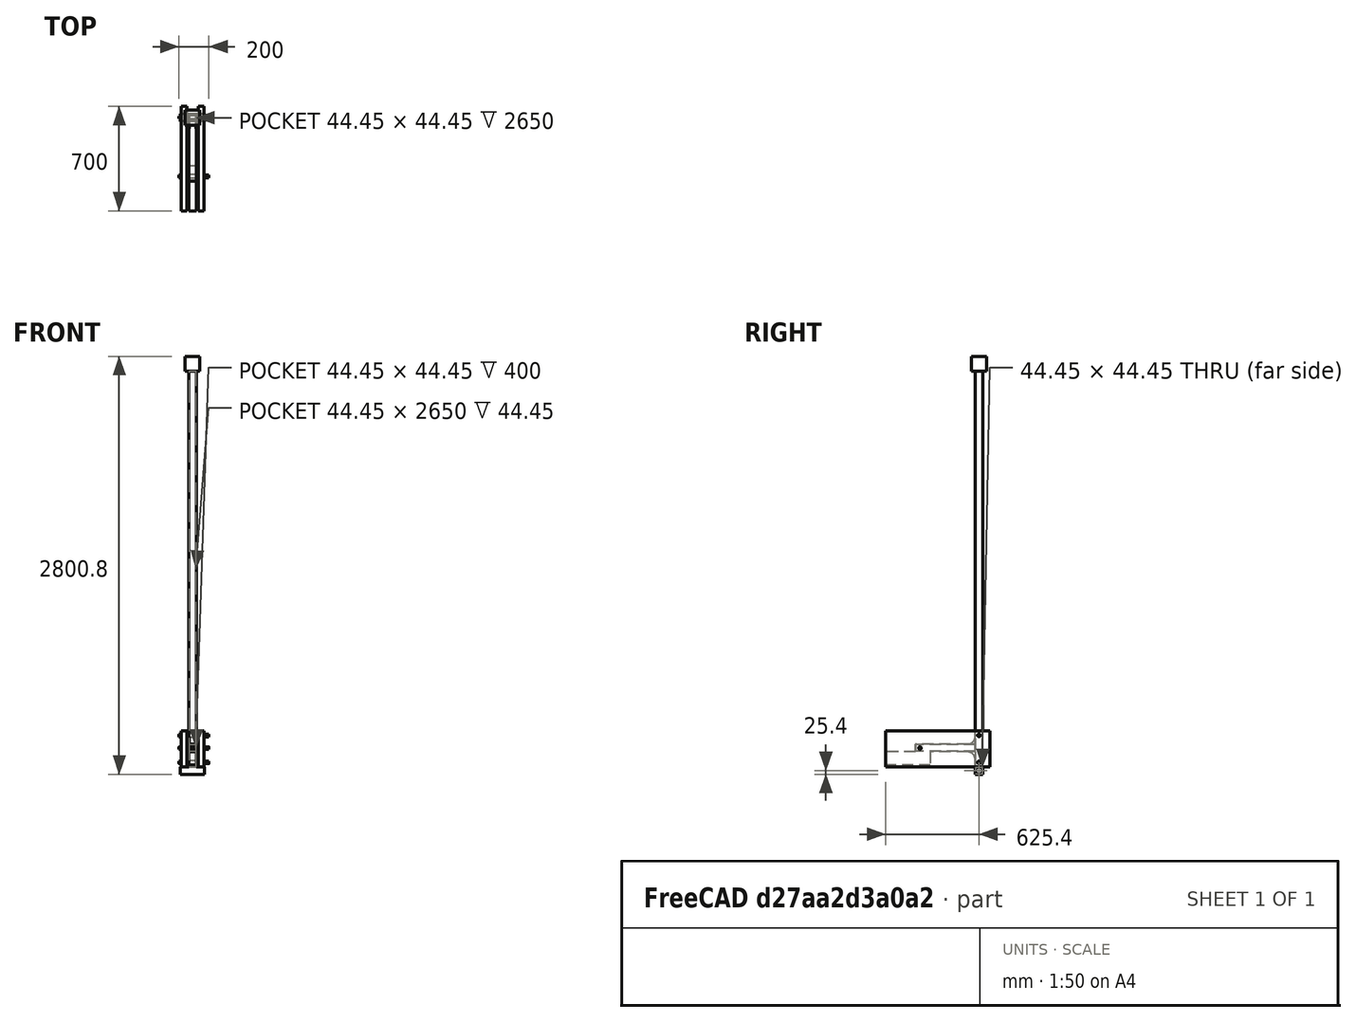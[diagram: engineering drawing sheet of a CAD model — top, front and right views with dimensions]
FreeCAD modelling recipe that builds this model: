
FCSTD DOCUMENT  (FreeCAD 0.16R6706 (Git))
Label: deckPost
License: All rights reserved
LicenseURL: http://en.wikipedia.org/wiki/All_rights_reserved
objects: Sketcher::SketchObject×19, PartDesign::Pad×19, Part::MultiFuse×6, Part::Cut×3, Part::Part2DObjectPython×2, Fem::ConstraintForce×2, Spreadsheet::Sheet×1, App::DocumentObjectGroup×1, Fem::FemSolverObjectPython×1, App::MaterialObjectPython×1, Part::Box×1, Fem::ConstraintFixed×1, Fem::FemAnalysisPython×1
note: 69 computed .brp shape members not serialized (recipe doc carries the construction recipe); baked Part::Feature solids carry a one-line shape summary decoded from their .brp

FEATURE [Sketcher::SketchObject] Sketch  label="TubeSketch"
  expr: Constraints[19] = Spreadsheet.wallThickness
  expr: Constraints[20] = Spreadsheet.wallThickness
  expr: Constraints[21] = Spreadsheet.outerWidth
  expr: Constraints[18] = Spreadsheet.wallThickness
  sketch-geometry (8):
    g0: LineSegment StartX=0 StartY=50.8 StartZ=0 EndX=50.8 EndY=50.8 EndZ=0
    g1: LineSegment StartX=50.8 StartY=50.8 StartZ=0 EndX=50.8 EndY=0 EndZ=0
    g2: LineSegment StartX=50.8 StartY=0 StartZ=0 EndX=0 EndY=0 EndZ=0
    g3: LineSegment StartX=0 StartY=0 StartZ=0 EndX=0 EndY=50.8 EndZ=0
    g4: LineSegment StartX=3.175 StartY=47.625 StartZ=0 EndX=47.625 EndY=47.625 EndZ=0
    g5: LineSegment StartX=47.625 StartY=47.625 StartZ=0 EndX=47.625 EndY=3.175 EndZ=0
    g6: LineSegment StartX=47.625 StartY=3.175 StartZ=0 EndX=3.175 EndY=3.175 EndZ=0
    g7: LineSegment StartX=3.175 StartY=3.175 StartZ=0 EndX=3.175 EndY=47.625 EndZ=0
  constraints (23):
    c: Coincident(g0,g1)
    c: Coincident(g1,g2)
    c: Coincident(g2,g3)
    c: Coincident(g3,g0)
    c: Horizontal(g0)
    c: Horizontal(g2)
    c: Vertical(g1)
    c: Vertical(g3)
    c: Coincident(g4,g5)
    c: Coincident(g5,g6)
    c: Coincident(g6,g7)
    c: Coincident(g7,g4)
    c: Horizontal(g4)
    c: Horizontal(g6)
    c: Vertical(g5)
    c: Vertical(g7)
    c: Equal(g0,g3)
    c: Equal(g4,g7)
    c: DistanceX(g0,g4) = 3.175
    c: DistanceY(g4,g0) = 3.175
    c: DistanceX(g5,g1) = 3.175
    c: Distance(g0,g0) = 50.8
    c: Coincident(g2,g-1)
FEATURE [PartDesign::Pad] Pad  label="Post"
  Length = 2650
  Length2 = 100
  Sketch = -> Sketch
  Type = 0
  expr: Length = Spreadsheet.postLength
FEATURE [Spreadsheet::Sheet] Spreadsheet
  cells = J2=N; K2=lbf; L2=Resultant Force lbf; A3=Tube Wall Thickness; B3(wallThickness)=3.175; C3==Spreadsheet.wallThickness; I3=Post Top Medial Force; J3(medialForce)=350; K3==medialForce / 9.810000000000001; L3==sqrt(Spreadsheet.medialForce ^ 2 + Spreadsheet.lateralForce ^ 2) / 9.810000000000001 * 2.2; A4=Tube Outer Width; B4(outerWidth)=50.8; C4==Spreadsheet.outerWidth; I4=8ft Post Lateral Force; J4(lateralForce)=350; K4==lateralForce / 9.810000000000001; A5=Brace Height; B5(braceHeight)=100; C5==Spreadsheet.braceHeight; A6=Brace Length; B6(braceLength)=400; C6==Spreadsheet.braceLength; A7=Bolt Hole Diam; B7(boltHoleDiam)=17; C7==Spreadsheet.boltHoleDiam; A8=Bolt Tube Thickness; B8(boltTubeThick)=3.175; C8==Spreadsheet.boltTubeThick; A9=Gusset Thickness; B9(gussetThickness)=3.175; C9==Spreadsheet.gussetThickness; A10=Upper Bolt Height; B10(upperBoltHeight)=210; C10==Spreadsheet.upperBoltHeight; D10==Spreadsheet.joistWidth - Spreadsheet.upperBoltHeight - Spreadsheet.boltHoleDiam / 2; E10==Spreadsheet.joistWidth - Spreadsheet.upperBoltHeight - Spreadsheet.boltHoleDiam / 2; F10=Distance from upper bolt hole to joist upper edge ; A11=Lower Bolt Height; B11(lowerBoltHeight)=30; C11==Spreadsheet.lowerBoltHeight; D11==Spreadsheet.lowerBoltHeight - Spreadsheet.boltHoleDiam / 2; E11==Spreadsheet.lowerBoltHeight - Spreadsheet.boltHoleDiam / 2; F11=Distance from lower bolt hole to joist lower edge; A12=Total Post Length; B12(postLength)=2650; C12==Spreadsheet.postLength; D12(postEffortArm)==Spreadsheet.postLength - Spreadsheet.joistWidth - Spreadsheet.deckThickness; E12==Spreadsheet.postLength - Spreadsheet.joistWidth - Spreadsheet.deckThickness; F12=Height Above Finished Deck; A13=2x10 Joist Width; B13(joistWidth)=241.3; C13==Spreadsheet.joistWidth; A14=Deck Thickness; B14(deckThickness)=19.05; C14==Spreadsheet.deckThickness; A15=Gusset Raduis; B15(gussetRadius)=75; C15==Spreadsheet.gussetRadius; A16=Gusset Length; B16(gussetLength)=50; C16==Spreadsheet.gussetLength; C19=Al 6061 - 0; D19=Al 6061 - T6; E19=ASTM A500 Steel Hot Rolled; I19=Douglas Fir; A20=Young's Modulus; C20==69GPa; D20==69GPa; E20==200GPa; I20==12.17GPa; A21=Poisson's Ratio; C21=0.33; D21=0.33; E21=0.29; I21=0.02; A22=Density; C22=2.7e-006; D22=2.7e-006; E22==7.85g / cm ^ 3; I22==510kg / m ^ 3; A23=Yield Strength; C23==55.2MPa; D23==276MPa; E23==270MPa; I23==3MPa; A24=Web Site; C24=http://www.matweb.com/search/DataSheet.aspx?MatGUID=626ec8cdca604f1994be4fc2bc6f7f63&ckck=1; D24=http://www.matweb.com/search/DataSheet.aspx?MatGUID=b8d536e0b9b54bd7b69e4124d8f1d20a; I24=http://www.wood-database.com/douglas-fir/
FEATURE [Sketcher::SketchObject] Sketch002  label="GussetSketch"
  Placement = pos=(0,0,150.8) rot=(0.57735,0.57735,0.57735;2.0944rad)
  expr: Constraints[9] = Spreadsheet.gussetRadius
  expr: Constraints[6] = Spreadsheet.gussetLength
  expr: Constraints[5] = Spreadsheet.gussetLength
  expr: Placement.Base.z = Spreadsheet.braceHeight + Spreadsheet.outerWidth
  sketch-geometry (3):
    g0: LineSegment StartX=0 StartY=0 StartZ=0 EndX=0 EndY=50 EndZ=0
    g1: LineSegment StartX=0 StartY=0 StartZ=0 EndX=-50 EndY=0 EndZ=0
    g2: ArcOfCircle CenterX=-53.033 CenterY=53.033 CenterZ=0 NormalX=0 NormalY=0 NormalZ=1 Radius=53.1197 StartAngle=4.76952 EndAngle=6.22606
  constraints (10):
    c: Vertical(g0)
    c: Coincident(g1,g0)
    c: PointOnObject(g1,g-1)
    c: Horizontal(g1)
    c: PointOnObject(g0,g-2)
    c: Distance(g0) = 50
    c: Distance(g1) = 50
    c: Coincident(g2,g0)
    c: Coincident(g2,g1)
    c: Distance(g-1,g2) = 75
FEATURE [PartDesign::Pad] Pad002  label="Gusset1"
  Length = 3.175
  Length2 = 100
  Placement = pos=(0,0,150.8) rot=(0.57735,0.57735,0.57735;2.0944rad)
  Sketch = -> Sketch002
  Type = 0
  expr: Length = Spreadsheet.gussetThickness
FEATURE [Sketcher::SketchObject] MirroredSketch
  Placement = pos=(0,0,100) rot=(0.57735,0.57735,0.57735;2.0944rad)
  expr: Constraints[3] = Spreadsheet.gussetLength
  expr: Constraints[7] = Spreadsheet.gussetRadius
  expr: Constraints[8] = Spreadsheet.gussetLength
  sketch-geometry (3):
    g0: LineSegment StartX=0 StartY=0 StartZ=0 EndX=0 EndY=-50 EndZ=0
    g1: LineSegment StartX=0 StartY=0 StartZ=0 EndX=-50 EndY=0 EndZ=0
    g2: ArcOfCircle CenterX=-53.033 CenterY=-53.033 CenterZ=0 NormalX=0 NormalY=0 NormalZ=1 Radius=53.1197 StartAngle=0.0571287 EndAngle=1.51367
  constraints (9):
    c: Vertical(g0)
    c: Coincident(g1,g0)
    c: Horizontal(g1)
    c: Distance(g0) = 50
    c: Coincident(g2,g0)
    c: Coincident(g0,g-1)
    c: Coincident(g1,g2)
    c: Distance(g-1,g2) = 75
    c: Distance(g1) = 50
FEATURE [PartDesign::Pad] Pad004  label="Gusset2"
  Length = 3.175
  Length2 = 100
  Placement = pos=(0,0,100) rot=(0.57735,0.57735,0.57735;2.0944rad)
  Sketch = -> MirroredSketch
  Type = 0
  expr: Length = Spreadsheet.gussetThickness
FEATURE [Sketcher::SketchObject] Sketch003  label="GussetSketch001"
  Placement = pos=(47.625,0,150.8) rot=(0.57735,0.57735,0.57735;2.0944rad)
  expr: Constraints[9] = Spreadsheet.gussetRadius
  expr: Placement.Base.x = Spreadsheet.outerWidth - Spreadsheet.gussetThickness
  expr: Constraints[6] = Spreadsheet.gussetLength
  expr: Constraints[5] = Spreadsheet.gussetLength
  expr: Placement.Base.z = Spreadsheet.braceHeight + Spreadsheet.outerWidth
  sketch-geometry (3):
    g0: LineSegment StartX=0 StartY=0 StartZ=0 EndX=0 EndY=50 EndZ=0
    g1: LineSegment StartX=0 StartY=0 StartZ=0 EndX=-50 EndY=0 EndZ=0
    g2: ArcOfCircle CenterX=-53.033 CenterY=53.033 CenterZ=0 NormalX=0 NormalY=0 NormalZ=1 Radius=53.1197 StartAngle=4.76952 EndAngle=6.22606
  constraints (10):
    c: Vertical(g0)
    c: Coincident(g1,g0)
    c: PointOnObject(g1,g-1)
    c: Horizontal(g1)
    c: PointOnObject(g0,g-2)
    c: Distance(g0) = 50
    c: Distance(g1) = 50
    c: Coincident(g2,g0)
    c: Coincident(g1,g2)
    c: Distance(g-1,g2) = 75
FEATURE [PartDesign::Pad] Pad005  label="Gusset3"
  Length = 3.175
  Length2 = 100
  Placement = pos=(47.625,0,150.8) rot=(0.57735,0.57735,0.57735;2.0944rad)
  Sketch = -> Sketch003
  Type = 0
  expr: Length = Spreadsheet.gussetThickness
FEATURE [Sketcher::SketchObject] MirroredSketch001
  Placement = pos=(47.625,0,100) rot=(0.57735,0.57735,0.57735;2.0944rad)
  expr: Constraints[8] = Spreadsheet.gussetRadius
  expr: Constraints[3] = Spreadsheet.gussetLength
  expr: Constraints[4] = Spreadsheet.gussetLength
  expr: Placement.Base.x = Spreadsheet.outerWidth - Spreadsheet.gussetThickness
  sketch-geometry (3):
    g0: LineSegment StartX=0 StartY=0 StartZ=0 EndX=0 EndY=-50 EndZ=0
    g1: LineSegment StartX=0 StartY=0 StartZ=0 EndX=-50 EndY=0 EndZ=0
    g2: ArcOfCircle CenterX=-53.033 CenterY=-53.033 CenterZ=0 NormalX=0 NormalY=0 NormalZ=1 Radius=53.1197 StartAngle=0.0571287 EndAngle=1.51367
  constraints (9):
    c: Vertical(g0)
    c: Coincident(g1,g0)
    c: Horizontal(g1)
    c: Distance(g0) = 50
    c: Distance(g1) = 50
    c: Coincident(g2,g1)
    c: Coincident(g0,g2)
    c: Coincident(g0,g-1)
    c: Distance(g-1,g2) = 75
FEATURE [PartDesign::Pad] Pad006  label="Gusset4"
  Length = 3.175
  Length2 = 100
  Placement = pos=(47.625,0,100) rot=(0.57735,0.57735,0.57735;2.0944rad)
  Sketch = -> MirroredSketch001
  Type = 0
  expr: Length = Spreadsheet.gussetThickness
FEATURE [Sketcher::SketchObject] Sketch004  label="Brace Bolt Tube Sketch"
  Placement = pos=(0,-370,125.4) rot=(0,1,0;1.5708rad)
  expr: Placement.Base.z = Spreadsheet.braceHeight + Spreadsheet.outerWidth / 2
  expr: Placement.Base.y = -Spreadsheet.braceLength + 30
  expr: Constraints[3] = Spreadsheet.boltHoleDiam / 2 + Spreadsheet.boltTubeThick
  expr: Constraints[2] = Spreadsheet.boltHoleDiam / 2
  sketch-geometry (2):
    g0: Circle CenterX=0 CenterY=0 CenterZ=0 NormalX=0 NormalY=0 NormalZ=1 Radius=8.5
    g1: Circle CenterX=0 CenterY=0 CenterZ=0 NormalX=0 NormalY=0 NormalZ=1 Radius=11.675
  constraints (4):
    c: Coincident(g0,g-1)
    c: Coincident(g1,g-1)
    c: Radius(g0) = 8.5
    c: Radius(g1) = 11.675
FEATURE [Part::Part2DObjectPython] Line  label="Brace Center"  # Draft 2D object (typed FeaturePython)
  ChamferSize = 0
  Closed = false
  End = (0,-300,131.75)
  FilletRadius = 0
  Length = 300
  MakeFace = false
  Placement = pos=(0,0,0) rot=(0,-1,0;1.5708rad)
  Points = (2) [(131.75,-8.10463e-15,2.92544e-14),(131.75,-300,-3.7359e-14)]
  Start = (0,0,131.75)
  Subdivisions = 0
FEATURE [Part::Part2DObjectPython] Line001  label="Post Ceenter"  # Draft 2D object (typed FeaturePython)
  ChamferSize = 0
  Closed = false
  End = (0,31.75,2500)
  FilletRadius = 0
  Length = 2500
  MakeFace = false
  Placement = pos=(0,0,0) rot=(0,-1,0;1.5708rad)
  Points = (2) [(0,31.75,0),(2500,31.75,5.62161e-13)]
  Start = (0,31.75,0)
  Subdivisions = 0
FEATURE [App::DocumentObjectGroup] Construction
  Group = -> [Line,Line001]
FEATURE [PartDesign::Pad] Pad007  label="Brace Bolt Tube"
  Length = 50.8
  Length2 = 100
  Placement = pos=(0,-370,125.4) rot=(0,1,0;1.5708rad)
  Sketch = -> Sketch004
  Type = 0
  expr: Length = Spreadsheet.outerWidth
FEATURE [Sketcher::SketchObject] Sketch005  label="Bolt Hole Sketch"
  Placement = pos=(0,-370,125.4) rot=(0,1,0;1.5708rad)
  expr: Placement.Base.y = -Spreadsheet.braceLength + 30
  expr: Placement.Base.z = Spreadsheet.braceHeight + Spreadsheet.outerWidth / 2
  sketch-geometry (1):
    g0: Circle CenterX=0 CenterY=0 CenterZ=0 NormalX=0 NormalY=0 NormalZ=1 Radius=9
  constraints (2):
    c: Coincident(g0,g-1)
    c: Radius(g0) = 9
FEATURE [PartDesign::Pad] Pad008  label="Brace Bolt Hole"
  Length = 50.8
  Length2 = 100
  Placement = pos=(0,-370,125.4) rot=(0,1,0;1.5708rad)
  Sketch = -> Sketch005
  Type = 0
  expr: Length = Spreadsheet.outerWidth
FEATURE [Sketcher::SketchObject] Sketch006  label="Lower Bolt Tube Sketch"
  Placement = pos=(0,25.4,30) rot=(0,1,0;1.5708rad)
  expr: Placement.Base.y = Spreadsheet.outerWidth / 2
  expr: Constraints[3] = Spreadsheet.boltHoleDiam / 2 + Spreadsheet.boltTubeThick
  expr: Constraints[2] = Spreadsheet.boltHoleDiam / 2
  sketch-geometry (2):
    g0: Circle CenterX=0 CenterY=0 CenterZ=0 NormalX=0 NormalY=0 NormalZ=1 Radius=8.5
    g1: Circle CenterX=0 CenterY=0 CenterZ=0 NormalX=0 NormalY=0 NormalZ=1 Radius=11.675
  constraints (4):
    c: Coincident(g0,g-1)
    c: Coincident(g1,g-1)
    c: Radius(g0) = 8.5
    c: Radius(g1) = 11.675
FEATURE [PartDesign::Pad] Pad009  label="Lower Bolt Tube"
  Length = 50.8
  Length2 = 100
  Placement = pos=(0,25.4,30) rot=(0,1,0;1.5708rad)
  Sketch = -> Sketch006
  Type = 0
  expr: Length = Spreadsheet.outerWidth
FEATURE [Sketcher::SketchObject] Sketch007  label="Upper Bolt Tube Sketch"
  Placement = pos=(0,25.4,210) rot=(0,1,0;1.5708rad)
  expr: Placement.Base.z = Spreadsheet.upperBoltHeight
  expr: Placement.Base.y = Spreadsheet.outerWidth / 2
  expr: Constraints[3] = Spreadsheet.boltHoleDiam / 2 + Spreadsheet.boltTubeThick
  expr: Constraints[2] = Spreadsheet.boltHoleDiam / 2
  sketch-geometry (2):
    g0: Circle CenterX=0 CenterY=0 CenterZ=0 NormalX=0 NormalY=0 NormalZ=1 Radius=8.5
    g1: Circle CenterX=0 CenterY=0 CenterZ=0 NormalX=0 NormalY=0 NormalZ=1 Radius=11.675
  constraints (4):
    c: Coincident(g0,g-1)
    c: Coincident(g1,g-1)
    c: Radius(g0) = 8.5
    c: Radius(g1) = 11.675
FEATURE [PartDesign::Pad] Pad010  label="Upper Bolt Tube"
  Length = 50.8
  Length2 = 100
  Placement = pos=(0,25.4,210) rot=(0,1,0;1.5708rad)
  Sketch = -> Sketch007
  Type = 0
  expr: Length = Spreadsheet.outerWidth
FEATURE [Sketcher::SketchObject] Sketch001  label="BraceTubeSketch"
  Placement = pos=(0,0,100) rot=(1,0,0;1.5708rad)
  expr: Placement.Base.z = Spreadsheet.braceHeight
  expr: Constraints[19] = Spreadsheet.wallThickness
  expr: Constraints[20] = Spreadsheet.wallThickness
  expr: Constraints[21] = Spreadsheet.outerWidth
  expr: Constraints[18] = Spreadsheet.wallThickness
  sketch-geometry (8):
    g0: LineSegment StartX=0 StartY=50.8 StartZ=0 EndX=50.8 EndY=50.8 EndZ=0
    g1: LineSegment StartX=50.8 StartY=50.8 StartZ=0 EndX=50.8 EndY=0 EndZ=0
    g2: LineSegment StartX=50.8 StartY=0 StartZ=0 EndX=0 EndY=0 EndZ=0
    g3: LineSegment StartX=0 StartY=0 StartZ=0 EndX=0 EndY=50.8 EndZ=0
    g4: LineSegment StartX=3.175 StartY=47.625 StartZ=0 EndX=47.625 EndY=47.625 EndZ=0
    g5: LineSegment StartX=47.625 StartY=47.625 StartZ=0 EndX=47.625 EndY=3.175 EndZ=0
    g6: LineSegment StartX=47.625 StartY=3.175 StartZ=0 EndX=3.175 EndY=3.175 EndZ=0
    g7: LineSegment StartX=3.175 StartY=3.175 StartZ=0 EndX=3.175 EndY=47.625 EndZ=0
  constraints (23):
    c: Coincident(g0,g1)
    c: Coincident(g1,g2)
    c: Coincident(g2,g3)
    c: Coincident(g3,g0)
    c: Horizontal(g0)
    c: Horizontal(g2)
    c: Vertical(g1)
    c: Vertical(g3)
    c: Coincident(g4,g5)
    c: Coincident(g5,g6)
    c: Coincident(g6,g7)
    c: Coincident(g7,g4)
    c: Horizontal(g4)
    c: Horizontal(g6)
    c: Vertical(g5)
    c: Vertical(g7)
    c: Equal(g0,g3)
    c: Equal(g4,g7)
    c: DistanceX(g0,g4) = 3.175
    c: DistanceY(g4,g0) = 3.175
    c: DistanceX(g5,g1) = 3.175
    c: Distance(g0,g0) = 50.8
    c: Coincident(g2,g-1)
FEATURE [PartDesign::Pad] Pad001  label="Brace"
  Length = 400
  Length2 = 100
  Placement = pos=(0,0,100) rot=(1,0,0;1.5708rad)
  Sketch = -> Sketch001
  Type = 0
  expr: Length = Spreadsheet.braceLength
FEATURE [Part::Cut] Cut  label="Brace Cut"
  Base = -> Pad001
  Tool = -> Pad008
FEATURE [Sketcher::SketchObject] Sketch008  label="Lower Bolt Hole Sketch"
  Placement = pos=(0,25.4,30) rot=(0,1,0;1.5708rad)
  expr: Placement.Base.y = Spreadsheet.outerWidth / 2
  sketch-geometry (1):
    g0: Circle CenterX=0 CenterY=0 CenterZ=0 NormalX=0 NormalY=0 NormalZ=1 Radius=9
  constraints (2):
    c: Coincident(g0,g-1)
    c: Radius(g0) = 9
FEATURE [PartDesign::Pad] Pad011  label="Lower Bolt Hole"
  Length = 50.8
  Length2 = 100
  Placement = pos=(0,25.4,30) rot=(0,1,0;1.5708rad)
  Sketch = -> Sketch008
  Type = 0
  expr: Length = Spreadsheet.outerWidth
FEATURE [Part::Cut] Cut001
  Base = -> Pad
  Tool = -> Pad011
FEATURE [Sketcher::SketchObject] Sketch009  label="Upper Bolt Hole Sketch"
  Placement = pos=(0,25.4,210) rot=(0,1,0;1.5708rad)
  expr: Placement.Base.z = Spreadsheet.upperBoltHeight
  expr: Placement.Base.y = Spreadsheet.outerWidth / 2
  sketch-geometry (1):
    g0: Circle CenterX=0 CenterY=0 CenterZ=0 NormalX=0 NormalY=0 NormalZ=1 Radius=9
  constraints (2):
    c: Coincident(g0,g-1)
    c: Radius(g0) = 9
FEATURE [PartDesign::Pad] Pad012  label="Upper Bolt Hole"
  Length = 50.8
  Length2 = 100
  Placement = pos=(0,25.4,210) rot=(0,1,0;1.5708rad)
  Sketch = -> Sketch009
  Type = 0
  expr: Length = Spreadsheet.outerWidth
FEATURE [Part::Cut] Cut002  label="Post Cut"
  Base = -> Cut001
  Tool = -> Pad012
FEATURE [Part::MultiFuse] Fusion  label="Brace Fusion"
  Shapes = -> [Cut,Pad007]
FEATURE [Part::MultiFuse] Fusion001  label="Post Fusion"
  Shapes = -> [Cut002,Pad009,Pad010]
FEATURE [Part::MultiFuse] Fusion002  label="Post and Bracket"
  Shapes = -> [Pad006,Pad005,Pad004,Pad002,Fusion,Fusion001]
FEATURE [Sketcher::SketchObject] Sketch010  label="Joist Sketch"
  Placement = pos=(-50.8,100,0) rot=(1,0,0;1.5708rad)
  expr: Placement.Base.x = -1.5in - 0.5in
  expr: Constraints[10] = Spreadsheet.joistWidth
  sketch-geometry (4):
    g0: LineSegment StartX=0 StartY=0 StartZ=0 EndX=38.1 EndY=0 EndZ=0
    g1: LineSegment StartX=38.1 StartY=0 StartZ=0 EndX=38.1 EndY=241.3 EndZ=0
    g2: LineSegment StartX=38.1 StartY=241.3 StartZ=0 EndX=0 EndY=241.3 EndZ=0
    g3: LineSegment StartX=0 StartY=241.3 StartZ=0 EndX=0 EndY=0 EndZ=0
  constraints (11):
    c: Coincident(g0,g1)
    c: Coincident(g1,g2)
    c: Coincident(g2,g3)
    c: Coincident(g3,g0)
    c: Horizontal(g0)
    c: Horizontal(g2)
    c: Vertical(g1)
    c: Vertical(g3)
    c: Coincident(g0,g-1)
    c: Distance(g2) = 38.1
    c: Distance(g3) = 241.3
FEATURE [PartDesign::Pad] Pad013  label="Joist"
  Length = 700
  Length2 = 100
  Placement = pos=(-50.8,100,0) rot=(1,0,0;1.5708rad)
  Sketch = -> Sketch010
  Type = 0
FEATURE [Sketcher::SketchObject] Sketch011  label="Brace Bolt Sketch"
  Placement = pos=(-65,-370,125.4) rot=(0,1,0;1.5708rad)
  expr: Placement.Base.y = -Spreadsheet.braceLength + 30
  expr: Placement.Base.z = Spreadsheet.braceHeight + Spreadsheet.outerWidth / 2
  sketch-geometry (1):
    g0: Circle CenterX=0 CenterY=0 CenterZ=0 NormalX=0 NormalY=0 NormalZ=1 Radius=9
  constraints (2):
    c: Coincident(g0,g-1)
    c: Radius(g0) = 9
FEATURE [PartDesign::Pad] Pad014  label="Brace Bolt"
  Length = 200
  Length2 = 100
  Placement = pos=(-65,-370,125.4) rot=(0,1,0;1.5708rad)
  Sketch = -> Sketch011
  Type = 0
FEATURE [Sketcher::SketchObject] Sketch012  label="Upper Bolt Sketch"
  Placement = pos=(-65,25.4,210) rot=(0,1,0;1.5708rad)
  expr: Placement.Base.y = Spreadsheet.outerWidth / 2
  expr: Placement.Base.z = Spreadsheet.upperBoltHeight
  sketch-geometry (1):
    g0: Circle CenterX=0 CenterY=0 CenterZ=0 NormalX=0 NormalY=0 NormalZ=1 Radius=9
  constraints (2):
    c: Coincident(g0,g-1)
    c: Radius(g0) = 9
FEATURE [PartDesign::Pad] Pad015  label="Upper Bolt"
  Length = 200
  Length2 = 100
  Placement = pos=(-65,25.4,210) rot=(0,1,0;1.5708rad)
  Sketch = -> Sketch012
  Type = 0
FEATURE [Sketcher::SketchObject] Sketch013  label="Lower Bolt Sketch"
  Placement = pos=(-65,25.4,30) rot=(0,1,0;1.5708rad)
  expr: Placement.Base.y = Spreadsheet.outerWidth / 2
  expr: Placement.Base.z = Spreadsheet.lowerBoltHeight
  sketch-geometry (1):
    g0: Circle CenterX=0 CenterY=0 CenterZ=0 NormalX=0 NormalY=0 NormalZ=1 Radius=9
  constraints (2):
    c: Coincident(g0,g-1)
    c: Radius(g0) = 9
FEATURE [PartDesign::Pad] Pad016  label="Lower Bolt"
  Length = 200
  Length2 = 100
  Placement = pos=(-65,25.4,30) rot=(0,1,0;1.5708rad)
  Sketch = -> Sketch013
  Type = 0
FEATURE [Sketcher::SketchObject] Sketch014  label="Lower support Tube Sketch"
  Placement = pos=(105,0,0) rot=(0,1,0;1.5708rad)
  expr: Constraints[19] = Spreadsheet.wallThickness
  expr: Constraints[20] = Spreadsheet.wallThickness
  expr: Constraints[21] = Spreadsheet.outerWidth
  expr: Constraints[18] = Spreadsheet.wallThickness
  sketch-geometry (8):
    g0: LineSegment StartX=0 StartY=50.8 StartZ=0 EndX=50.8 EndY=50.8 EndZ=0
    g1: LineSegment StartX=50.8 StartY=50.8 StartZ=0 EndX=50.8 EndY=0 EndZ=0
    g2: LineSegment StartX=50.8 StartY=0 StartZ=0 EndX=0 EndY=0 EndZ=0
    g3: LineSegment StartX=0 StartY=0 StartZ=0 EndX=0 EndY=50.8 EndZ=0
    g4: LineSegment StartX=3.175 StartY=47.625 StartZ=0 EndX=47.625 EndY=47.625 EndZ=0
    g5: LineSegment StartX=47.625 StartY=47.625 StartZ=0 EndX=47.625 EndY=3.175 EndZ=0
    g6: LineSegment StartX=47.625 StartY=3.175 StartZ=0 EndX=3.175 EndY=3.175 EndZ=0
    g7: LineSegment StartX=3.175 StartY=3.175 StartZ=0 EndX=3.175 EndY=47.625 EndZ=0
  constraints (23):
    c: Coincident(g0,g1)
    c: Coincident(g1,g2)
    c: Coincident(g2,g3)
    c: Coincident(g3,g0)
    c: Horizontal(g0)
    c: Horizontal(g2)
    c: Vertical(g1)
    c: Vertical(g3)
    c: Coincident(g4,g5)
    c: Coincident(g5,g6)
    c: Coincident(g6,g7)
    c: Coincident(g7,g4)
    c: Horizontal(g4)
    c: Horizontal(g6)
    c: Vertical(g5)
    c: Vertical(g7)
    c: Equal(g0,g3)
    c: Equal(g4,g7)
    c: DistanceX(g0,g4) = 3.175
    c: DistanceY(g4,g0) = 3.175
    c: DistanceX(g5,g1) = 3.175
    c: Distance(g0,g0) = 50.8
    c: Coincident(g2,g-1)
FEATURE [PartDesign::Pad] Pad017  label="Lower support Tube"
  Length = 160
  Length2 = 100
  Placement = pos=(105,0,0) rot=(0,1,0;1.5708rad)
  Reversed = true
  Sketch = -> Sketch014
  Type = 0
FEATURE [Sketcher::SketchObject] Sketch015  label="Joist 2 Sketch"
  Placement = pos=(62.8,100,0) rot=(1,0,0;1.5708rad)
  expr: Placement.Base.x = Spreadsheet.outerWidth + 12
  expr: Constraints[10] = Spreadsheet.joistWidth
  sketch-geometry (4):
    g0: LineSegment StartX=0 StartY=0 StartZ=0 EndX=38.1 EndY=0 EndZ=0
    g1: LineSegment StartX=38.1 StartY=0 StartZ=0 EndX=38.1 EndY=241.3 EndZ=0
    g2: LineSegment StartX=38.1 StartY=241.3 StartZ=0 EndX=0 EndY=241.3 EndZ=0
    g3: LineSegment StartX=0 StartY=241.3 StartZ=0 EndX=0 EndY=0 EndZ=0
  constraints (11):
    c: Coincident(g0,g1)
    c: Coincident(g1,g2)
    c: Coincident(g2,g3)
    c: Coincident(g3,g0)
    c: Horizontal(g0)
    c: Horizontal(g2)
    c: Vertical(g1)
    c: Vertical(g3)
    c: Coincident(g0,g-1)
    c: Distance(g2) = 38.1
    c: Distance(g3) = 241.3
FEATURE [PartDesign::Pad] Pad018  label="Joist 2"
  Length = 700
  Length2 = 100
  Placement = pos=(62.8,100,0) rot=(1,0,0;1.5708rad)
  Sketch = -> Sketch015
  Type = 0
FEATURE [Sketcher::SketchObject] Sketch016  label="Brace Support Sketch"
  Placement = pos=(0,-300,11.1) rot=(1,0,0;1.5708rad)
  expr: Placement.Base.z = Spreadsheet.braceHeight - 3.5 * 25.4
  expr: Constraints[9] = Spreadsheet.outerWidth
  expr: Constraints[10] = 3.5in
  sketch-geometry (4):
    g0: LineSegment StartX=0 StartY=0 StartZ=0 EndX=50.8 EndY=0 EndZ=0
    g1: LineSegment StartX=50.8 StartY=0 StartZ=0 EndX=50.8 EndY=88.9 EndZ=0
    g2: LineSegment StartX=50.8 StartY=88.9 StartZ=0 EndX=0 EndY=88.9 EndZ=0
    g3: LineSegment StartX=0 StartY=88.9 StartZ=0 EndX=0 EndY=0 EndZ=0
  constraints (11):
    c: Coincident(g0,g1)
    c: Coincident(g1,g2)
    c: Coincident(g2,g3)
    c: Coincident(g3,g0)
    c: Horizontal(g0)
    c: Horizontal(g2)
    c: Vertical(g1)
    c: Vertical(g3)
    c: Coincident(g0,g-1)
    c: Distance(g2) = 50.8
    c: Distance(g3) = 88.9
FEATURE [PartDesign::Pad] Pad019  label="Brace Support"
  Length = 300
  Length2 = 100
  Placement = pos=(0,-300,11.1) rot=(1,0,0;1.5708rad)
  Sketch = -> Sketch016
  Type = 0
FEATURE [Part::MultiFuse] Fusion003
  Shapes = -> [Fusion002,Pad013,Pad014,Pad017,Pad018,Pad019]
FEATURE [Fem::FemSolverObjectPython] CalculiX  # FEM object (typed FeaturePython)
  AnalysisType = 0
  EigenmodeHighLimit = 1000000
  EigenmodeLowLimit = 0
  NumberOfEigenmodes = 10
  SolverType = FemSolverCalculix
FEATURE [App::MaterialObjectPython] MechanicalMaterial  # material (typed FeaturePython)
  Material = Density=7850.0 kg/m^3,Description=This is a not defined material,Father=None,Name=None,PoissonRatio=0.29,SpecificPrice=0,+2 more (map truncated)
FEATURE [Part::Box] Box  label="Cube"
  Height = 100
  Length = 100
  Placement = pos=(-25,-25,2650) rot=(0,0,1;0rad)
  Width = 100
FEATURE [Fem::ConstraintForce] FemConstraintForce  label="FemConstraintMedialForce"
  DirectionVector = (0,-1,0)
  Force = 500
  NormalDirection = (0,1,0)
  Points = (16) [(-25,75,2650),(-25,75,2683.33),(-25,75,2716.67),(-25,75,2750),(8.33333,75,2650),(8.33333,75,2683.33),(8.33333,75,2716.67),(8.33333,75,2750),+8 more]
  References = -> [Box]
  Reversed = true
  Scale = 10
FEATURE [Part::MultiFuse] Fusion004
  Shapes = -> [Fusion003,Box]
FEATURE [Fem::ConstraintFixed] FemConstraintFixed
  NormalDirection = (0,-1,0)
  Normals = (48) [(0,-1,6.79661e-16),(0,-1,6.79661e-16),(0,-1,6.79661e-16),(0,-1,6.79661e-16),(0,-1,6.79661e-16),(0,-1,6.79661e-16),(0,-1,6.79661e-16),+41 more]
  Points = (48) [(-50.8,-600,3.10862e-13),(-50.8,-600,80.4333),(-50.8,-600,160.867),(-50.8,-600,241.3),(-38.1,-600,3.10862e-13),(-38.1,-600,80.4333),+42 more]
  References = -> [Fusion004]
  Scale = 12
FEATURE [Fem::ConstraintForce] FemConstraintForce001  label="FemConstraintLateralForce"
  DirectionVector = (-1,0,0)
  Force = 1
  NormalDirection = (1,0,0)
  Points = (16) [(75,75,2650),(75,75,2683.33),(75,75,2716.67),(75,75,2750),(75,41.6667,2650),(75,41.6667,2683.33),(75,41.6667,2716.67),(75,41.6667,2750),+8 more]
  References = -> [Fusion004]
  Reversed = true
  Scale = 10
FEATURE [Fem::FemAnalysisPython] MechanicalAnalysis  # FEM object (typed FeaturePython)
  Member = -> [CalculiX,MechanicalMaterial,FemConstraintFixed,FemConstraintForce,FemConstraintForce001]
FEATURE [Part::MultiFuse] Fusion005
  Shapes = -> [Pad015,Pad016,Fusion004]
